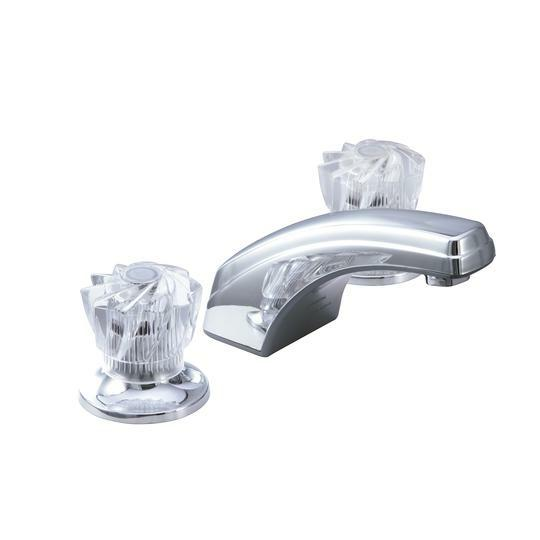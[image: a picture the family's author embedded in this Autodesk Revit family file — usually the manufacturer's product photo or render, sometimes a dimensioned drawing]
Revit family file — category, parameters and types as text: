
# Revit family: 01-1103-00 MEZCLADOR LAVAMANOS 8” KRISTHAL
name_source: partatom
category: Plumbing Fixtures
revit_build: Autodesk Revit 2018 (Build: 20170223_1515(x64)
units: mm (PartAtom-declared; Revit-internal decimal feet)

## family parameters
Cut with Voids When Loaded = No
Host = Face
OmniClass Number = 23.31.11.00
Part Type = Normal
Room Calculation Point = No
Round Connector Dimension = Use Diameter
Shared = No

## types (1)
- 01-1103-00
    Alto = 90.7 mm
    Alto - Aireador = 68.5 mm
    CW Connection = Yes
    Default Elevation = 0 mm  [stored 0 ft]
    Description = Bimando baño
    Eje ( Rosca) = 203.2 mm  [stored 0.666667 ft]
    Eje-Aireador = 122.6 mm  [stored 0.402231 ft]
    HW Connection = Yes
    Link Ficha Tecnica = https://infotecnica.gricol.com
    Manufacturer = Gricol
    Model = 01-1103-00
    Plastico - ABS Cromado = Plastico - ABS Cromado
    Plastico acrilico transparente = Plastico Acrilico Transparente
    Product Name = MEZCLADOR LAVAMANOS 8” KRISTHAL
    Type Image = MEZCLADOR LAVAMANOS 8” KRISTHAL.jpg
    URL = https://www.gricol.com
    Vent Connection = No
    Waste Connection = No

note: [stored X ft] marks values corroborated as IEEE doubles in the binary element streams (Revit-internal decimal feet)

## geometry (parser evidence)
native form markers: Blend x2, Sweep x2
no freeform markers — native parametric forms only
